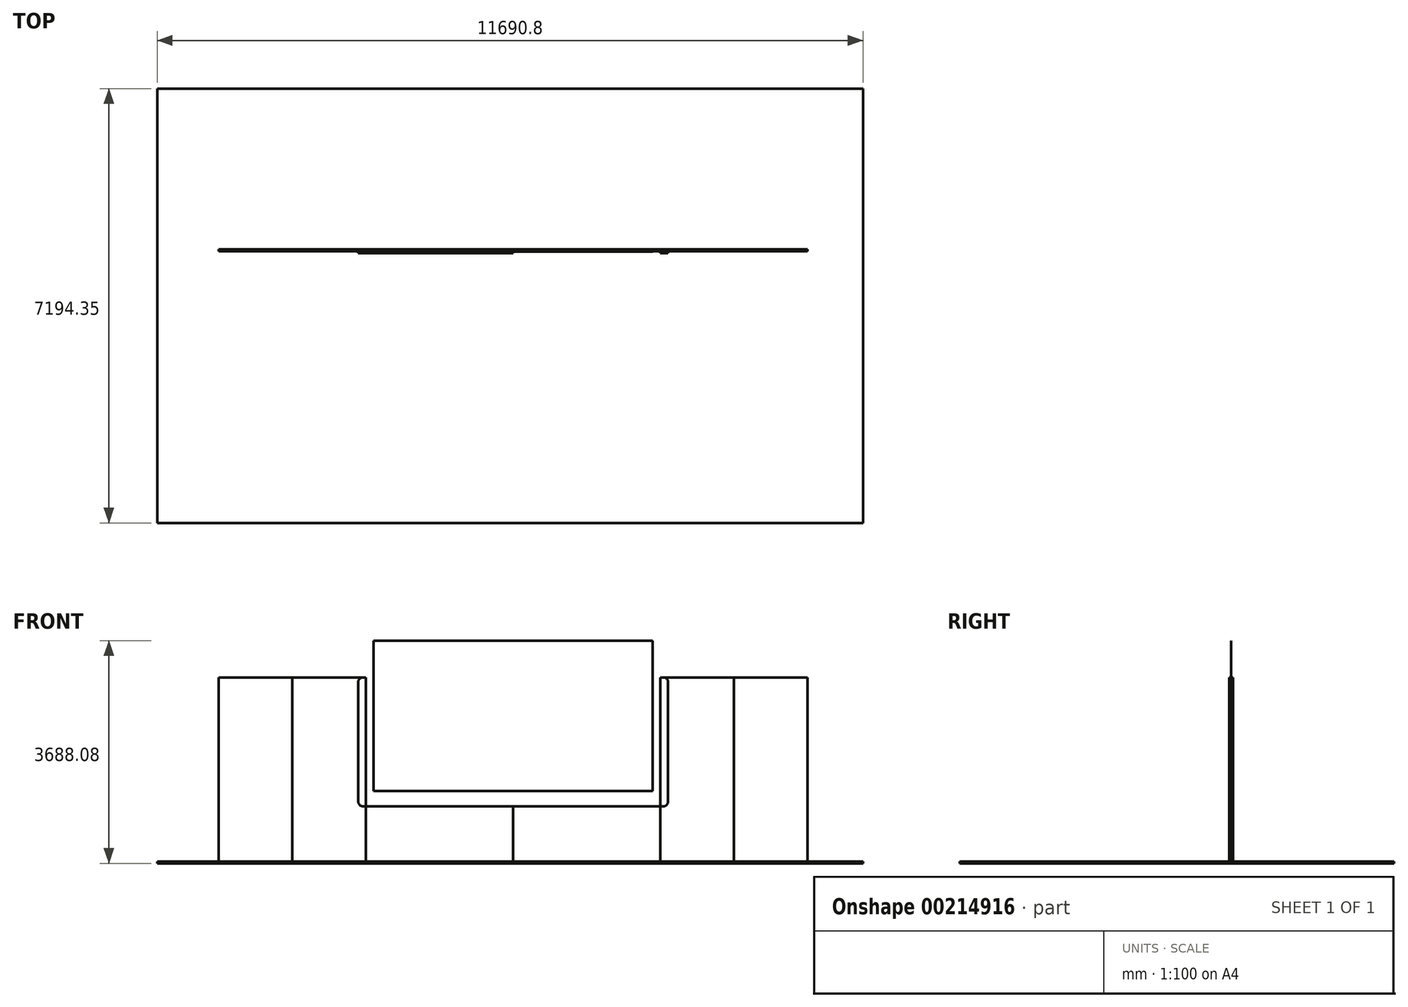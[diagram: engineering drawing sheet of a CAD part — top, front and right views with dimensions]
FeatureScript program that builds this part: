
annotation { "Feature Type Name" : "Feature", "Feature Type Description" : "" }
export const myFeature = defineFeature(function(context is Context, id is Id, definition is map)
    precondition{}
    {
        {
            var Q0;
            Q0=qCreatedBy(makeId("Front.planeOp"),FACE);
            var sketch = newSketch(context, id + "F0", { "sketchPlane" : qUnion([Q0])});
            skLineSegment(sketch, "E0.bottom", {"start": v(0, 0) * mm, "end": v(1219.2, 0) * mm});
            skLineSegment(sketch, "E0.top", {"start": v(0, 3048) * mm, "end": v(1219.2, 3048) * mm});
            skLineSegment(sketch, "E0.left", {"start": v(0, 0) * mm, "end": v(0, 3048) * mm});
            skLineSegment(sketch, "E0.right", {"start": v(1219.2, 0) * mm, "end": v(1219.2, 3048) * mm});
            skLineSegment(sketch, "E1.bottom", {"start": v(1219.2, 0) * mm, "end": v(2438.4, 0) * mm});
            skLineSegment(sketch, "E1.top", {"start": v(1219.2, 3048) * mm, "end": v(2438.4, 3048) * mm});
            skLineSegment(sketch, "E1.right", {"start": v(2438.4, 0) * mm, "end": v(2438.4, 3048) * mm});
            skLineSegment(sketch, "E2.bottom", {"start": v(2438.4, 0) * mm, "end": v(4876.8, 0) * mm});
            skLineSegment(sketch, "E2.top", {"start": v(2438.4, 914.4) * mm, "end": v(4876.8, 914.4) * mm});
            skLineSegment(sketch, "E2.left", {"start": v(2438.4, 0) * mm, "end": v(2438.4, 914.4) * mm});
            skLineSegment(sketch, "E2.right", {"start": v(4876.8, 0) * mm, "end": v(4876.8, 914.4) * mm});
            skLineSegment(sketch, "E3.bottom", {"start": v(4876.8, 0) * mm, "end": v(7315.2, 0) * mm});
            skLineSegment(sketch, "E3.top", {"start": v(4876.8, 914.4) * mm, "end": v(7315.2, 914.4) * mm});
            skLineSegment(sketch, "E3.right", {"start": v(7315.2, 0) * mm, "end": v(7315.2, 914.4) * mm});
            skLineSegment(sketch, "E4.bottom", {"start": v(7315.2, 0) * mm, "end": v(8534.4, 0) * mm});
            skLineSegment(sketch, "E4.top", {"start": v(7315.2, 3048) * mm, "end": v(8534.4, 3048) * mm});
            skLineSegment(sketch, "E4.left", {"start": v(7315.2, 0) * mm, "end": v(7315.2, 3048) * mm});
            skLineSegment(sketch, "E4.right", {"start": v(8534.4, 0) * mm, "end": v(8534.4, 3048) * mm});
            skLineSegment(sketch, "E5.bottom", {"start": v(8534.4, 0) * mm, "end": v(9753.6, 0) * mm});
            skLineSegment(sketch, "E5.top", {"start": v(8534.4, 3048) * mm, "end": v(9753.6, 3048) * mm});
            skLineSegment(sketch, "E5.right", {"start": v(9753.6, 0) * mm, "end": v(9753.6, 3048) * mm});
            skLineSegment(sketch, "E6.bottom", {"start": v(2311.4, 914.4) * mm, "end": v(7442.2, 914.4) * mm});
            skLineSegment(sketch, "E6.top", {"start": v(2311.4, 3911.6) * mm, "end": v(7442.2, 3911.6) * mm});
            skLineSegment(sketch, "E6.left", {"start": v(2311.4, 914.4) * mm, "end": v(2311.4, 3911.6) * mm});
            skLineSegment(sketch, "E6.right", {"start": v(7442.2, 914.4) * mm, "end": v(7442.2, 3911.6) * mm});
            skPoint(sketch, "E6.middle", {"position": v(4876.8, 2413) * mm});
            skLineSegment(sketch, "E7.0", {"start": v(2565.4, 3657.6) * mm, "end": v(7188.2, 3657.6) * mm});
            skLineSegment(sketch, "E7.1", {"start": v(2565.4, 1168.4) * mm, "end": v(2565.4, 3657.6) * mm});
            skLineSegment(sketch, "E7.2", {"start": v(2565.4, 1168.4) * mm, "end": v(7188.2, 1168.4) * mm});
            skLineSegment(sketch, "E7.3", {"start": v(7188.2, 1168.4) * mm, "end": v(7188.2, 3657.6) * mm});
            skLineSegment(sketch, "E8", {"start": v(4876.8, 3657.6) * mm, "end": v(4876.8, 3911.6) * mm, "construction": true});
            skLineSegment(sketch, "E9", {"start": v(4876.8, 1168.4) * mm, "end": v(4876.8, 914.4) * mm, "construction": true});
            skLineSegment(sketch, "E10", {"start": v(7188.2, 2413) * mm, "end": v(7442.2, 2413) * mm, "construction": true});
            skLineSegment(sketch, "E11", {"start": v(2565.4, 2413) * mm, "end": v(2311.4, 2413) * mm, "construction": true});
            skPoint(sketch, "E12", {"position": v(4876.8, 3784.6) * mm});
            skPoint(sketch, "E13", {"position": v(4876.8, 1041.4) * mm});
            skPoint(sketch, "E14", {"position": v(2438.4, 2413) * mm});
            skPoint(sketch, "E15", {"position": v(7315.2, 2413) * mm});
            skLineSegment(sketch, "E16", {"start": v(2438.4, 2413) * mm, "end": v(2438.4, 914.4) * mm, "construction": true});
            skSolve(sketch);
        }
        {
            var Q0;
            Q0=makeQuery(id+"F0.imprint","IMPRINT",FACE,{"disambiguationData":[TD([[makeQuery(id+"F0.imprint","IMPRINT",EDGE,{"derivedFrom":sQuery(id+"F0.wireOp",EDGE,"E0.bottom")}),1.0]])]});
            var Q1;
            Q1=makeQuery(id+"F0.imprint","IMPRINT",FACE,{"disambiguationData":[TD([[makeQuery(id+"F0.imprint","IMPRINT",EDGE,{"derivedFrom":sQuery(id+"F0.wireOp",EDGE,"E2.bottom")}),1.0]])]});
            var Q2;
            {var subQ2=sQuery(id+"F0.wireOp",EDGE,"E4.bottom");Q2=makeQuery(id+"F0.imprint","IMPRINT",FACE,{"disambiguationData":[TD([[makeQuery(id+"F0.imprint","IMPRINT",EDGE,{"derivedFrom":subQ2}),1.0]])]});}
            var Q3;
            {var subQ0=sQuery(id+"F0.wireOp",EDGE,"E4.left");var subQ1=sQuery(id+"F0.wireOp",EDGE,"E4.top");var subQ2=makeQuery(id+"F0.imprint","INTERSECT",VERTEX,{"derivedFrom":[subQ1,subQ0]});Q3=makeQuery(id+"F0.imprint","IMPRINT",FACE,{"disambiguationData":[TD([[makeQuery(id+"F0.imprint","IMPRINT",EDGE,{"disambiguationData":[TD([[subQ2,-1.0]])],"derivedFrom":subQ1}),-1.0]])]});}
            extrude(context, id + "F1", {"entities" : qUnion([Q0, Q1, Q2, Q3]), "oppositeDirection" : true, "depth" : 30.48 * mm});
        }
        {
            var Q0;
            Q0=makeQuery(id+"F0.imprint","IMPRINT",FACE,{"disambiguationData":[TD([[makeQuery(id+"F0.imprint","IMPRINT",EDGE,{"derivedFrom":sQuery(id+"F0.wireOp",EDGE,"E1.bottom")}),1.0]])]});
            var Q1;
            {var subQ0=sQuery(id+"F0.wireOp",EDGE,"E1.right");Q1=makeQuery(id+"F0.imprint","IMPRINT",FACE,{"disambiguationData":[TD([[makeQuery(id+"F0.imprint","IMPRINT",EDGE,{"derivedFrom":subQ0}),1.0]])]});}
            var Q2;
            {var subQ0=sQuery(id+"F0.wireOp",EDGE,"E3.bottom");Q2=makeQuery(id+"F0.imprint","IMPRINT",FACE,{"disambiguationData":[TD([[makeQuery(id+"F0.imprint","IMPRINT",EDGE,{"derivedFrom":subQ0}),1.0]])]});}
            var Q3;
            Q3=makeQuery(id+"F0.imprint","IMPRINT",FACE,{"disambiguationData":[TD([[makeQuery(id+"F0.imprint","IMPRINT",EDGE,{"derivedFrom":sQuery(id+"F0.wireOp",EDGE,"E5.bottom")}),1.0]])]});
            extrude(context, id + "F2", {"entities" : qUnion([Q0, Q1, Q2, Q3]), "oppositeDirection" : true, "depth" : 30.48 * mm});
        }
        {
            var Q0;
            {var subQ11=sQuery(id+"F0.wireOp",EDGE,"E1.right");Q0=makeQuery(id+"F0.imprint","IMPRINT",FACE,{"disambiguationData":[TD([[makeQuery(id+"F0.imprint","IMPRINT",EDGE,{"derivedFrom":subQ11}),-1.0]])]});}
            var Q1;
            {var subQ0=sQuery(id+"F0.wireOp",EDGE,"E1.right");Q1=makeQuery(id+"F0.imprint","IMPRINT",FACE,{"disambiguationData":[TD([[makeQuery(id+"F0.imprint","IMPRINT",EDGE,{"derivedFrom":subQ0}),1.0]])]});}
            var Q2;
            {var subQ0=sQuery(id+"F0.wireOp",EDGE,"E4.left");var subQ1=sQuery(id+"F0.wireOp",EDGE,"E4.top");var subQ2=makeQuery(id+"F0.imprint","INTERSECT",VERTEX,{"derivedFrom":[subQ1,subQ0]});Q2=makeQuery(id+"F0.imprint","IMPRINT",FACE,{"disambiguationData":[TD([[makeQuery(id+"F0.imprint","IMPRINT",EDGE,{"disambiguationData":[TD([[subQ2,-1.0]])],"derivedFrom":subQ1}),-1.0]])]});}
            extrude(context, id + "F3", {"entities" : qUnion([Q0, Q1, Q2]), "depth" : 30.48 * mm});
        }
        {
            var Q0;
            Q0=makeQuery(id+"F0.imprint","IMPRINT",FACE,{"disambiguationData":[TD([[makeQuery(id+"F0.imprint","IMPRINT",EDGE,{"derivedFrom":sQuery(id+"F0.wireOp",EDGE,"E7.0")}),-1.0]])]});
            extrude(context, id + "F4", {"entities" : qUnion([Q0]), "depth" : 3.05 * mm});
        }
        {
            var Q0;
            Q0=makeQuery(id+"F3.opExtrude","SWEPT_EDGE",EDGE,{"disambiguationData":[OSD([sQuery(id+"F0.wireOp",EDGE,"E6.top"),sQuery(id+"F0.wireOp",EDGE,"E6.left")])]});
            var Q1;
            Q1=makeQuery(id+"F3.opExtrude","SWEPT_EDGE",EDGE,{"disambiguationData":[OSD([sQuery(id+"F0.wireOp",EDGE,"E7.0"),sQuery(id+"F0.wireOp",EDGE,"E7.1")])]});
            var Q2;
            Q2=makeQuery(id+"F3.opExtrude","SWEPT_EDGE",EDGE,{"disambiguationData":[OSD([sQuery(id+"F0.wireOp",EDGE,"E6.bottom"),sQuery(id+"F0.wireOp",EDGE,"E6.left")])]});
            var Q3;
            Q3=makeQuery(id+"F3.opExtrude","SWEPT_EDGE",EDGE,{"disambiguationData":[OSD([sQuery(id+"F0.wireOp",EDGE,"E7.1"),sQuery(id+"F0.wireOp",EDGE,"E7.2")])]});
            var Q4;
            Q4=makeQuery(id+"F3.opExtrude","SWEPT_EDGE",EDGE,{"disambiguationData":[OSD([sQuery(id+"F0.wireOp",EDGE,"E6.bottom"),sQuery(id+"F0.wireOp",EDGE,"E6.right")])]});
            var Q5;
            Q5=makeQuery(id+"F3.opExtrude","SWEPT_EDGE",EDGE,{"disambiguationData":[OSD([sQuery(id+"F0.wireOp",EDGE,"E7.2"),sQuery(id+"F0.wireOp",EDGE,"E7.3")])]});
            var Q6;
            Q6=makeQuery(id+"F3.opExtrude","SWEPT_EDGE",EDGE,{"disambiguationData":[OSD([sQuery(id+"F0.wireOp",EDGE,"E6.top"),sQuery(id+"F0.wireOp",EDGE,"E6.right")])]});
            var Q7;
            Q7=makeQuery(id+"F3.opExtrude","SWEPT_EDGE",EDGE,{"disambiguationData":[OSD([sQuery(id+"F0.wireOp",EDGE,"E7.0"),sQuery(id+"F0.wireOp",EDGE,"E7.3")])]});
            fillet(context, id + "F5", {"entities" : qUnion([Q0, Q1, Q2, Q3, Q4, Q5, Q6, Q7]), "radius" : 76.2 * mm, "tangentPropagation" : true, "allowEdgeOverflow" : false});
        }
        {
            var Q0;
            Q0=qCreatedBy(makeId("Top.planeOp"),FACE);
            var sketch = newSketch(context, id + "F6", { "sketchPlane" : qUnion([Q0])});
            skLineSegment(sketch, "E17.bottom", {"start": v(-1018.84, -4498.73) * mm, "end": v(10672, -4498.73) * mm});
            skLineSegment(sketch, "E17.top", {"start": v(-1018.84, 2695.62) * mm, "end": v(10672, 2695.62) * mm});
            skLineSegment(sketch, "E17.left", {"start": v(-1018.84, -4498.73) * mm, "end": v(-1018.84, 2695.62) * mm});
            skLineSegment(sketch, "E17.right", {"start": v(10672, -4498.73) * mm, "end": v(10672, 2695.62) * mm});
            skSolve(sketch);
        }
        {
            var Q0;
            Q0=makeQuery(id+"F6.imprint","IMPRINT",FACE,{"disambiguationData":[TD([[makeQuery(id+"F6.imprint","IMPRINT",EDGE,{"derivedFrom":sQuery(id+"F6.wireOp",EDGE,"E17.bottom")}),1.0]])]});
            var Q1;
            Q1=sQuery(id+"F6.wireOp",EDGE,"E17.bottom");
            extrude(context, id + "F7", {"entities" : qUnion([Q0]), "surfaceEntities" : qUnion([Q1]), "oppositeDirection" : true, "depth" : 30.48 * mm});
        }
    });
